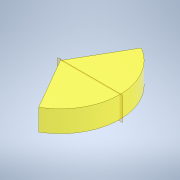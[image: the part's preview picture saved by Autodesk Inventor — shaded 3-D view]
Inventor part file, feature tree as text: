
AUTODESK INVENTOR PART (.ipt)
format: ipt  version: 2021.1 (Build 251245010, 245A)  size: 809,472 bytes
history: native  units: in
note: dims shown in document units (in); Inventor stores cm internally (conversion verified against a paired STEP export)
features: sketch x3, revolve x2, projected_geometry x2, plane x1, emboss x1, fillet x1
ambient origin geometry x8: Origin, YZ Plane, XZ Plane, XY Plane, X Axis, Y Axis, Z Axis, Center Point
bodies: Solid1 (feature_tree)
feature tree (10):
  revolve  "Revolution1"  [1 undecoded]
  plane  "Work Plane1"
  emboss  "Emboss1"
  revolve  "Revolution3"  [1 undecoded]
  fillet  "Fillet1"  [1 undecoded]
  sketch  "Sketch1"  dims[d2=0.25in d3=0.25in]
  sketch  "Sketch7"  dims[d4=4.5625in d5=1.5in d6=120.0deg]
  projected_geometry  "Projected Loop2"
  projected_geometry  "Projected Loop3"
  sketch  "Sketch8"  dims[d31=0.05in d32=0.0in d33=0.125in d34=3.0in d35=0.5in d37=120.0deg d38=0.0625in d20=1.0in d21=1.0in d22=1.0in d23=0.15in d24=0.25in d25=0.375in d26=0.5635in d27=0.75in d28=0.8108in d29=0.0625in d30=0.75in]
note: 3 required parameter values undecoded (feature->parameter linkage not recoverable at this tier; creation-order binding heuristic only, values carry confidence <= 0.55)